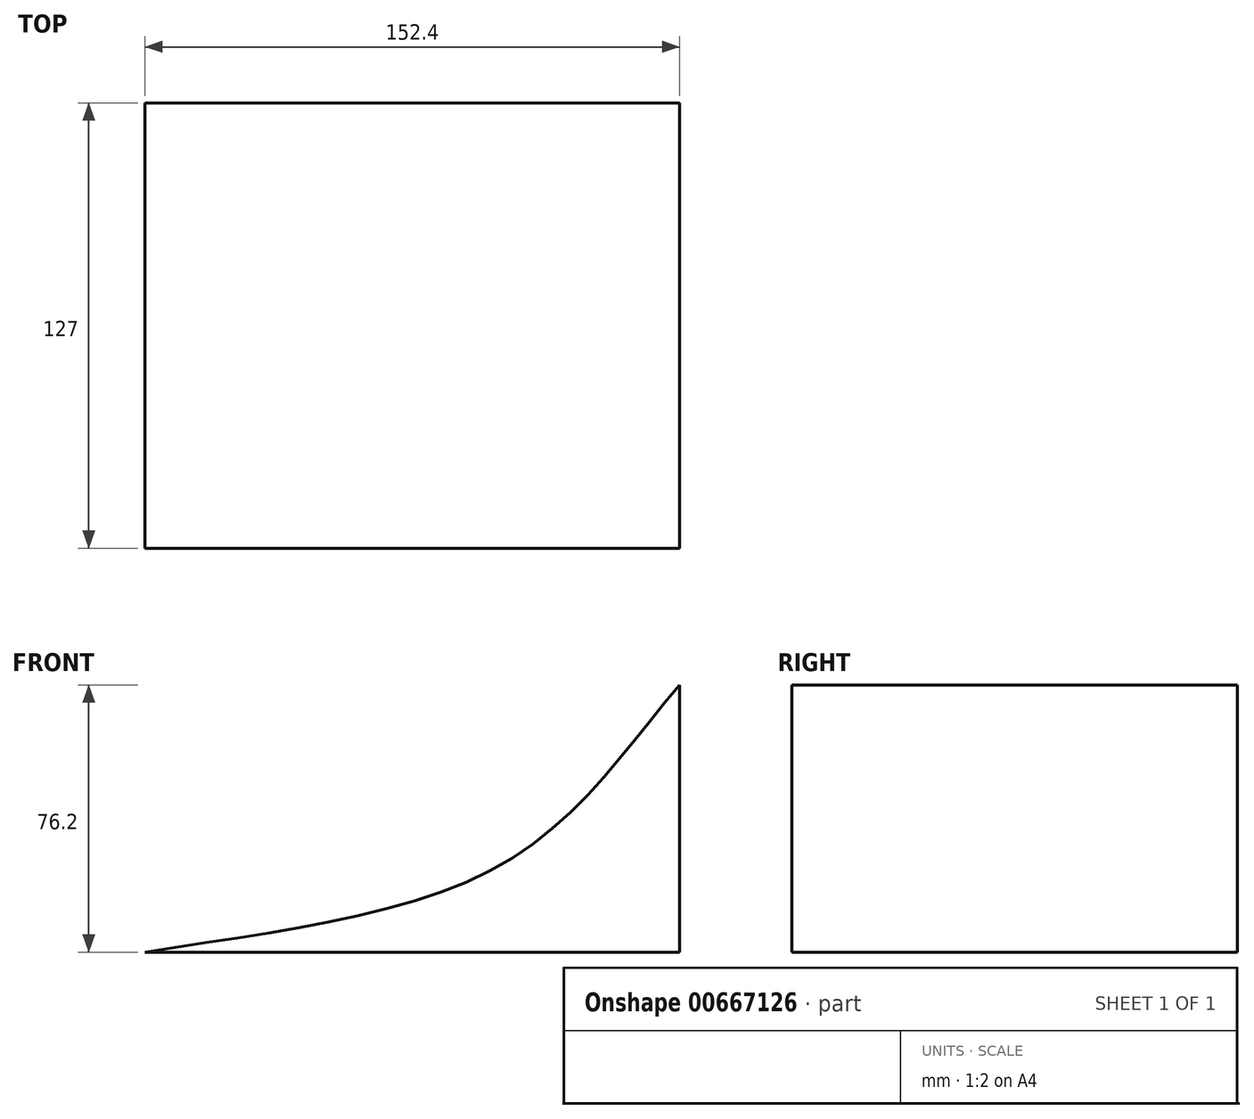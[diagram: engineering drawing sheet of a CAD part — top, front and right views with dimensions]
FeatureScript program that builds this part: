
annotation { "Feature Type Name" : "Feature", "Feature Type Description" : "" }
export const myFeature = defineFeature(function(context is Context, id is Id, definition is map)
    precondition{}
    {
        {
            var Q0;
            Q0=qCreatedBy(makeId("Front.planeOp"),FACE);
            var sketch = newSketch(context, id + "F0", { "sketchPlane" : qUnion([Q0])});
            skLineSegment(sketch, "E0", {"start": v(0, 0) * mm, "end": v(80.4, 0) * mm});
            skLineSegment(sketch, "E1", {"start": v(80.4, 0) * mm, "end": v(-72, 0) * mm});
            skLineSegment(sketch, "E2", {"start": v(80.4, 0) * mm, "end": v(80.4, 76.2) * mm});
            skPoint(sketch, "E3", {"position": v(30.3, 25.35) * mm});
            skFitSpline(sketch, "E4", {"points": [v(-72, 0) * mm, v(30.3, 25.35) * mm, v(80.4, 76.2) * mm], "startDerivative": vector(200.47, 32.33) * mm, "endDerivative": vector(99.14, 117.38) * mm});
            skSolve(sketch);
        }
        {
            var Q0;
            {var subQ0=sQuery(id+"F0.wireOp",EDGE,"E2");Q0=makeQuery(id+"F0.imprint","IMPRINT",FACE,{"disambiguationData":[TD([[makeQuery(id+"F0.imprint","IMPRINT",EDGE,{"derivedFrom":subQ0}),1.0]])]});}
            extrude(context, id + "F1", {"entities" : qUnion([Q0]), "depth" : 127 * mm, "offsetDistance" : 25.4 * mm});
        }
    });
